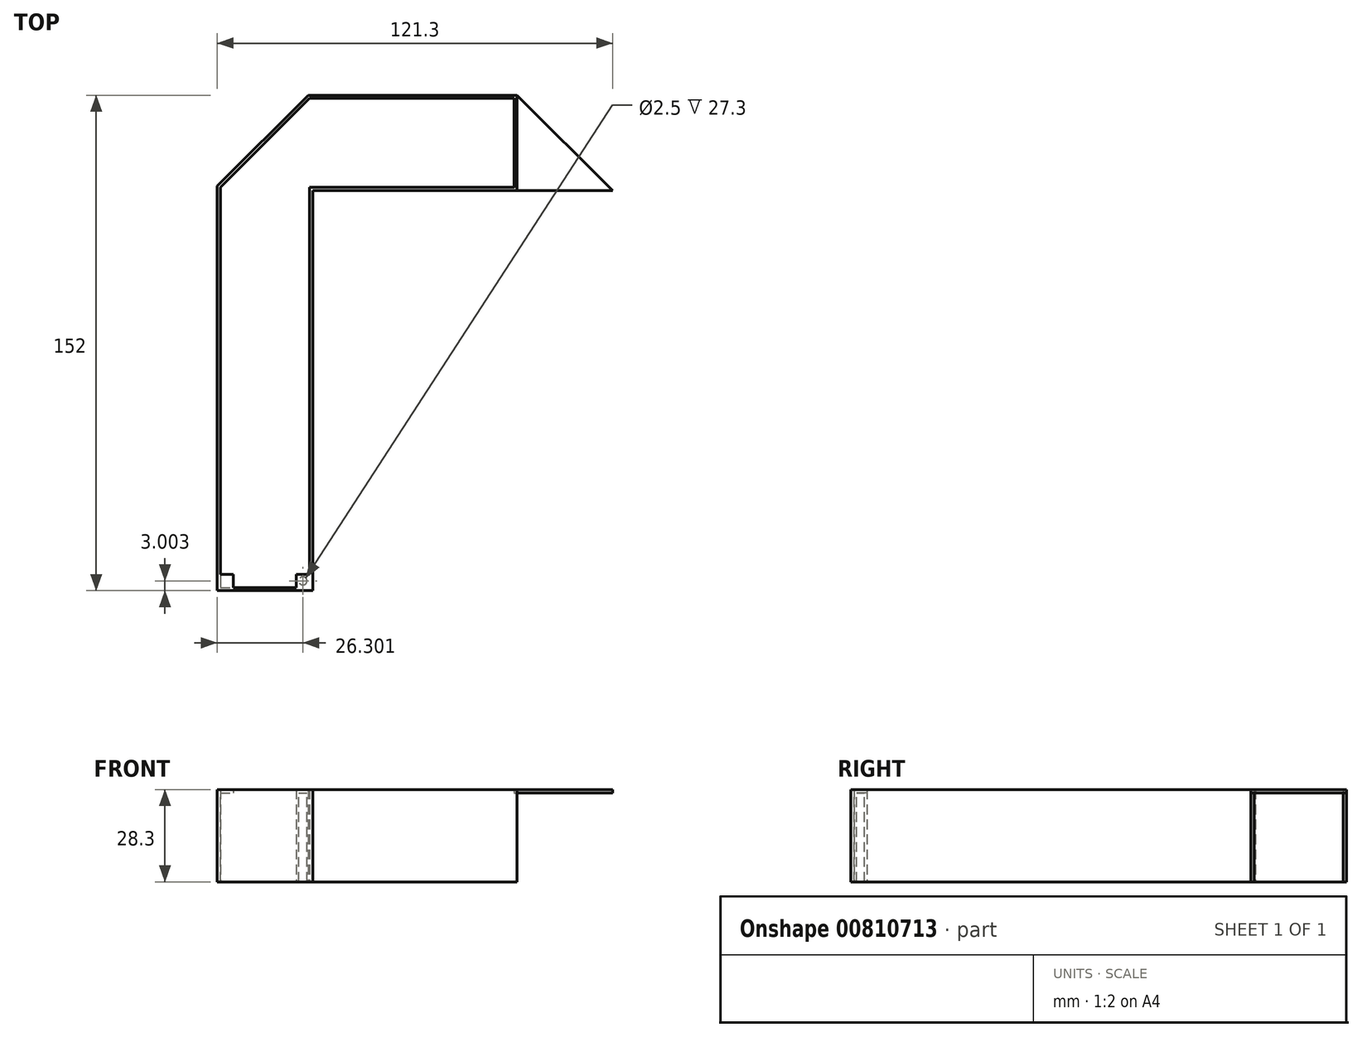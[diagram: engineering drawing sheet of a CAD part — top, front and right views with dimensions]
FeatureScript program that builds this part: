
annotation { "Feature Type Name" : "Feature", "Feature Type Description" : "" }
export const myFeature = defineFeature(function(context is Context, id is Id, definition is map)
    precondition{}
    {
        {
            assignVariable(context, id + "F0", {"name" : "larghezza_display", "anyValue" : 27.3 * mm});
        }
        {
            assignVariable(context, id + "F1", {"name" : "spessore_contenitore", "anyValue" : 1});
        }
        {
            var Q0;
            Q0=qCreatedBy(makeId("Top.planeOp"),FACE);
            var sketch = newSketch(context, id + "F2", { "sketchPlane" : qUnion([Q0])});
            skLineSegment(sketch, "E0", {"start": v(-57.05, -56.69) * mm, "end": v(-29.75, -56.69) * mm});
            skLineSegment(sketch, "E1", {"start": v(-29.75, -56.69) * mm, "end": v(-29.75, 66.01) * mm});
            skLineSegment(sketch, "E2", {"start": v(-29.75, 66.01) * mm, "end": v(32.95, 66.01) * mm});
            skLineSegment(sketch, "E3", {"start": v(32.95, 66.01) * mm, "end": v(32.95, 93.31) * mm});
            skLineSegment(sketch, "E4", {"start": v(32.95, 93.31) * mm, "end": v(-29.75, 93.31) * mm});
            skLineSegment(sketch, "E5", {"start": v(-29.75, 93.31) * mm, "end": v(-57.05, 66.01) * mm});
            skLineSegment(sketch, "E6", {"start": v(-57.05, 66.01) * mm, "end": v(-57.05, -56.69) * mm});
            skLineSegment(sketch, "E7.0", {"start": v(-30.16, 94.31) * mm, "end": v(-58.05, 66.43) * mm});
            skLineSegment(sketch, "E7.1", {"start": v(33.95, 94.31) * mm, "end": v(-30.16, 94.31) * mm});
            skLineSegment(sketch, "E7.2", {"start": v(-58.05, -57.69) * mm, "end": v(-28.75, -57.69) * mm});
            skLineSegment(sketch, "E7.3", {"start": v(-28.75, -57.69) * mm, "end": v(-28.75, 65.01) * mm});
            skLineSegment(sketch, "E7.4", {"start": v(-28.75, 65.01) * mm, "end": v(33.95, 65.01) * mm});
            skLineSegment(sketch, "E7.5", {"start": v(-58.05, 66.43) * mm, "end": v(-58.05, -57.69) * mm});
            skLineSegment(sketch, "E7.6", {"start": v(33.95, 65.01) * mm, "end": v(33.95, 94.31) * mm});
            skLineSegment(sketch, "E8.bottom", {"start": v(-57.05, -52.69) * mm, "end": v(-53.05, -52.69) * mm});
            skLineSegment(sketch, "E8.top", {"start": v(-57.05, -56.69) * mm, "end": v(-53.05, -56.69) * mm});
            skLineSegment(sketch, "E8.left", {"start": v(-57.05, -52.69) * mm, "end": v(-57.05, -56.69) * mm});
            skLineSegment(sketch, "E8.right", {"start": v(-53.05, -52.69) * mm, "end": v(-53.05, -56.69) * mm});
            skLineSegment(sketch, "E9.bottom", {"start": v(-29.75, -52.69) * mm, "end": v(-33.75, -52.69) * mm});
            skLineSegment(sketch, "E9.top", {"start": v(-29.75, -56.69) * mm, "end": v(-33.75, -56.69) * mm});
            skLineSegment(sketch, "E9.left", {"start": v(-29.75, -52.69) * mm, "end": v(-29.75, -56.69) * mm});
            skLineSegment(sketch, "E9.right", {"start": v(-33.75, -52.69) * mm, "end": v(-33.75, -56.69) * mm});
            skLineSegment(sketch, "E10", {"start": v(-57.05, -52.69) * mm, "end": v(-29.96, -52.69) * mm, "construction": true});
            skCircle(sketch, "E11", {"center": v(-55.05, -54.69) * mm, "radius": 1 * mm});
            skPoint(sketch, "E11.centerSnap0", {"position": v(-57.05, -54.69) * mm});
            skCircle(sketch, "E12", {"center": v(-31.75, -54.69) * mm, "radius": 1 * mm});
            skSolve(sketch);
        }
        {
            var Q0;
            Q0=makeQuery(id+"F2.imprint","IMPRINT",FACE,{"disambiguationData":[TD([[makeQuery(id+"F2.imprint","IMPRINT",EDGE,{"derivedFrom":sQuery(id+"F2.wireOp",EDGE,"E0")}),1.0]])]});
            var Q1;
            Q1=makeQuery(id+"F2.imprint","IMPRINT",FACE,{"disambiguationData":[TD([[makeQuery(id+"F2.imprint","IMPRINT",EDGE,{"derivedFrom":sQuery(id+"F2.wireOp",EDGE,"E0")}),-1.0]])]});
            var Q2;
            Q2=makeQuery(id+"F2.imprint","IMPRINT",FACE,{"disambiguationData":[TD([[makeQuery(id+"F2.imprint","IMPRINT",EDGE,{"derivedFrom":sQuery(id+"F2.wireOp",EDGE,"E12")}),1.0]])]});
            var Q3;
            Q3=makeQuery(id+"F2.imprint","IMPRINT",FACE,{"disambiguationData":[TD([[makeQuery(id+"F2.imprint","IMPRINT",EDGE,{"derivedFrom":sQuery(id+"F2.wireOp",EDGE,"E9.bottom")}),1.0]])]});
            var Q4;
            Q4=makeQuery(id+"F2.imprint","IMPRINT",FACE,{"disambiguationData":[TD([[makeQuery(id+"F2.imprint","IMPRINT",EDGE,{"derivedFrom":sQuery(id+"F2.wireOp",EDGE,"E8.bottom")}),-1.0]])]});
            var Q5;
            Q5=makeQuery(id+"F2.imprint","IMPRINT",FACE,{"disambiguationData":[TD([[makeQuery(id+"F2.imprint","IMPRINT",EDGE,{"derivedFrom":sQuery(id+"F2.wireOp",EDGE,"E11")}),1.0]])]});
            extrude(context, id + "F3", {"entities" : qUnion([Q0, Q1, Q2, Q3, Q4, Q5]), "depth" : (getVariable(context, 'spessore_contenitore')) * mm, "offsetDistance" : 25 * mm});
        }
        {
            var Q0;
            Q0 = qSketchRegion(id + "F2", true);
            extrude(context, id + "F4", {"entities" : qUnion([Q0]), "operationType" : NewBodyOperationType.ADD, "oppositeDirection" : true, "depth" : getVariable(context, 'larghezza_display'), "offsetDistance" : 25 * mm});
        }
        {
            var Q0;
            Q0=makeQuery(id+"F3.opExtrude","CAP_FACE",FACE,{"disambiguationData":[OSD([sQuery(id+"F2.wireOp",EDGE,"E7.0"),sQuery(id+"F2.wireOp",EDGE,"E7.1"),sQuery(id+"F2.wireOp",EDGE,"E7.2"),sQuery(id+"F2.wireOp",EDGE,"E7.3"),sQuery(id+"F2.wireOp",EDGE,"E7.4"),sQuery(id+"F2.wireOp",EDGE,"E7.5"),sQuery(id+"F2.wireOp",EDGE,"E7.6")])],"isStart":true});
            var sketch = newSketch(context, id + "F5", { "sketchPlane" : qUnion([Q0])});
            skLineSegment(sketch, "E13.bottom", {"start": v(-57.05, 56.69) * mm, "end": v(-53.05, 56.69) * mm});
            skLineSegment(sketch, "E13.top", {"start": v(-57.05, 52.69) * mm, "end": v(-53.05, 52.69) * mm});
            skLineSegment(sketch, "E13.left", {"start": v(-57.05, 56.69) * mm, "end": v(-57.05, 52.69) * mm});
            skLineSegment(sketch, "E13.right", {"start": v(-53.05, 56.69) * mm, "end": v(-53.05, 52.69) * mm});
            skLineSegment(sketch, "E14.bottom", {"start": v(-29.75, 56.69) * mm, "end": v(-33.75, 56.69) * mm});
            skLineSegment(sketch, "E14.top", {"start": v(-29.75, 52.69) * mm, "end": v(-33.75, 52.69) * mm});
            skLineSegment(sketch, "E14.left", {"start": v(-29.75, 56.69) * mm, "end": v(-29.75, 52.69) * mm});
            skLineSegment(sketch, "E14.right", {"start": v(-33.75, 56.69) * mm, "end": v(-33.75, 52.69) * mm});
            skCircle(sketch, "E15", {"center": v(-55.05, 54.69) * mm, "radius": 1.25 * mm});
            skCircle(sketch, "E16", {"center": v(-31.75, 54.69) * mm, "radius": 1.25 * mm});
            skSolve(sketch);
        }
        {
            var Q0;
            Q0=makeQuery(id+"F5.imprint","IMPRINT",FACE,{"disambiguationData":[TD([[makeQuery(id+"F5.imprint","IMPRINT",EDGE,{"derivedFrom":sQuery(id+"F5.wireOp",EDGE,"E13.bottom")}),1.0]])]});
            var Q1;
            Q1=makeQuery(id+"F5.imprint","IMPRINT",FACE,{"disambiguationData":[TD([[makeQuery(id+"F5.imprint","IMPRINT",EDGE,{"derivedFrom":sQuery(id+"F5.wireOp",EDGE,"E14.bottom")}),1.0]])]});
            extrude(context, id + "F6", {"entities" : qUnion([Q0, Q1]), "operationType" : NewBodyOperationType.ADD, "depth" : getVariable(context, 'larghezza_display'), "offsetDistance" : 25 * mm});
        }
        {
            var Q0;
            Q0=makeQuery(id+"F6.boolean.opBoolean","MERGE",FACE,{"derivedFrom":[makeQuery(id+"F4.opExtrude","CAP_FACE",FACE,{"disambiguationData":[OSD([sQuery(id+"F2.wireOp",EDGE,"E0"),sQuery(id+"F2.wireOp",EDGE,"E1"),sQuery(id+"F2.wireOp",EDGE,"E2"),sQuery(id+"F2.wireOp",EDGE,"E3"),sQuery(id+"F2.wireOp",EDGE,"E4"),sQuery(id+"F2.wireOp",EDGE,"E5"),sQuery(id+"F2.wireOp",EDGE,"E6"),sQuery(id+"F2.wireOp",EDGE,"E7.0"),sQuery(id+"F2.wireOp",EDGE,"E7.1"),sQuery(id+"F2.wireOp",EDGE,"E7.2"),sQuery(id+"F2.wireOp",EDGE,"E7.3"),sQuery(id+"F2.wireOp",EDGE,"E7.4"),sQuery(id+"F2.wireOp",EDGE,"E7.5"),sQuery(id+"F2.wireOp",EDGE,"E7.6"),sQuery(id+"F2.wireOp",EDGE,"E8.top"),sQuery(id+"F2.wireOp",EDGE,"E8.left"),sQuery(id+"F2.wireOp",EDGE,"E9.top"),sQuery(id+"F2.wireOp",EDGE,"E9.left")])],"isStart":false}),makeQuery(id+"F6.opExtrude","CAP_FACE",FACE,{"disambiguationData":[OSD([sQuery(id+"F5.wireOp",EDGE,"E13.bottom"),sQuery(id+"F5.wireOp",EDGE,"E13.top"),sQuery(id+"F5.wireOp",EDGE,"E13.left"),sQuery(id+"F5.wireOp",EDGE,"E13.right"),sQuery(id+"F5.wireOp",EDGE,"E15")])],"isStart":false}),makeQuery(id+"F6.opExtrude","CAP_FACE",FACE,{"disambiguationData":[OSD([sQuery(id+"F5.wireOp",EDGE,"E14.bottom"),sQuery(id+"F5.wireOp",EDGE,"E14.top"),sQuery(id+"F5.wireOp",EDGE,"E14.left"),sQuery(id+"F5.wireOp",EDGE,"E14.right"),sQuery(id+"F5.wireOp",EDGE,"E16")])],"isStart":false})]});
            var sketch = newSketch(context, id + "F7", { "sketchPlane" : qUnion([Q0])});
            skLineSegment(sketch, "E17.bottom", {"start": v(32.95, -66.01) * mm, "end": v(33.95, -66.01) * mm});
            skLineSegment(sketch, "E17.top", {"start": v(32.95, -93.31) * mm, "end": v(33.95, -93.31) * mm});
            skLineSegment(sketch, "E17.left", {"start": v(32.95, -66.01) * mm, "end": v(32.95, -93.31) * mm});
            skLineSegment(sketch, "E17.right", {"start": v(33.95, -66.01) * mm, "end": v(33.95, -93.31) * mm});
            skSolve(sketch);
        }
        {
            var Q0;
            Q0=makeQuery(id+"F7.imprint","IMPRINT",FACE,{"disambiguationData":[TD([[makeQuery(id+"F7.imprint","IMPRINT",EDGE,{"derivedFrom":sQuery(id+"F7.wireOp",EDGE,"E17.bottom")}),-1.0]])]});
            var Q1;
            Q1=makeQuery(id+"F6.boolean.opBoolean","SPLIT",FACE,{"disambiguationData":[TD([makeQuery(id+"F4.opExtrude","SWEPT_FACE",FACE,{"disambiguationData":[OSD([sQuery(id+"F2.wireOp",EDGE,"E2")])]})])],"derivedFrom":makeQuery(id+"F3.opExtrude","CAP_FACE",FACE,{"disambiguationData":[OSD([sQuery(id+"F2.wireOp",EDGE,"E7.0"),sQuery(id+"F2.wireOp",EDGE,"E7.1"),sQuery(id+"F2.wireOp",EDGE,"E7.2"),sQuery(id+"F2.wireOp",EDGE,"E7.3"),sQuery(id+"F2.wireOp",EDGE,"E7.4"),sQuery(id+"F2.wireOp",EDGE,"E7.5"),sQuery(id+"F2.wireOp",EDGE,"E7.6")])],"isStart":true})});
            extrude(context, id + "F8", {"entities" : qUnion([Q0]), "operationType" : NewBodyOperationType.REMOVE, "endBound" : BoundingType.UP_TO_SURFACE, "oppositeDirection" : true, "depth" : 25 * mm, "endBoundEntityFace" : qUnion([Q1]), "offsetDistance" : 25 * mm});
        }
        {
            var Q0;
            Q0=makeQuery(id+"F3.opExtrude","CAP_FACE",FACE,{"disambiguationData":[OSD([sQuery(id+"F2.wireOp",EDGE,"E7.0"),sQuery(id+"F2.wireOp",EDGE,"E7.1"),sQuery(id+"F2.wireOp",EDGE,"E7.2"),sQuery(id+"F2.wireOp",EDGE,"E7.3"),sQuery(id+"F2.wireOp",EDGE,"E7.4"),sQuery(id+"F2.wireOp",EDGE,"E7.5"),sQuery(id+"F2.wireOp",EDGE,"E7.6")])],"isStart":false});
            var sketch = newSketch(context, id + "F9", { "sketchPlane" : qUnion([Q0])});
            skLineSegment(sketch, "E18", {"start": v(33.95, 94.31) * mm, "end": v(33.95, 65.01) * mm});
            skLineSegment(sketch, "E19", {"start": v(33.95, 65.01) * mm, "end": v(63.25, 65.01) * mm});
            skLineSegment(sketch, "E20", {"start": v(63.25, 65.01) * mm, "end": v(33.95, 94.31) * mm});
            skSolve(sketch);
        }
        {
            var Q0;
            Q0=makeQuery(id+"F9.imprint","IMPRINT",FACE,{"disambiguationData":[TD([[makeQuery(id+"F9.imprint","IMPRINT",EDGE,{"derivedFrom":sQuery(id+"F9.wireOp",EDGE,"E18")}),-1.0]])]});
            extrude(context, id + "F10", {"entities" : qUnion([Q0]), "oppositeDirection" : true, "depth" : (getVariable(context, 'spessore_contenitore')) * mm, "offsetDistance" : 25 * mm});
        }
    });
